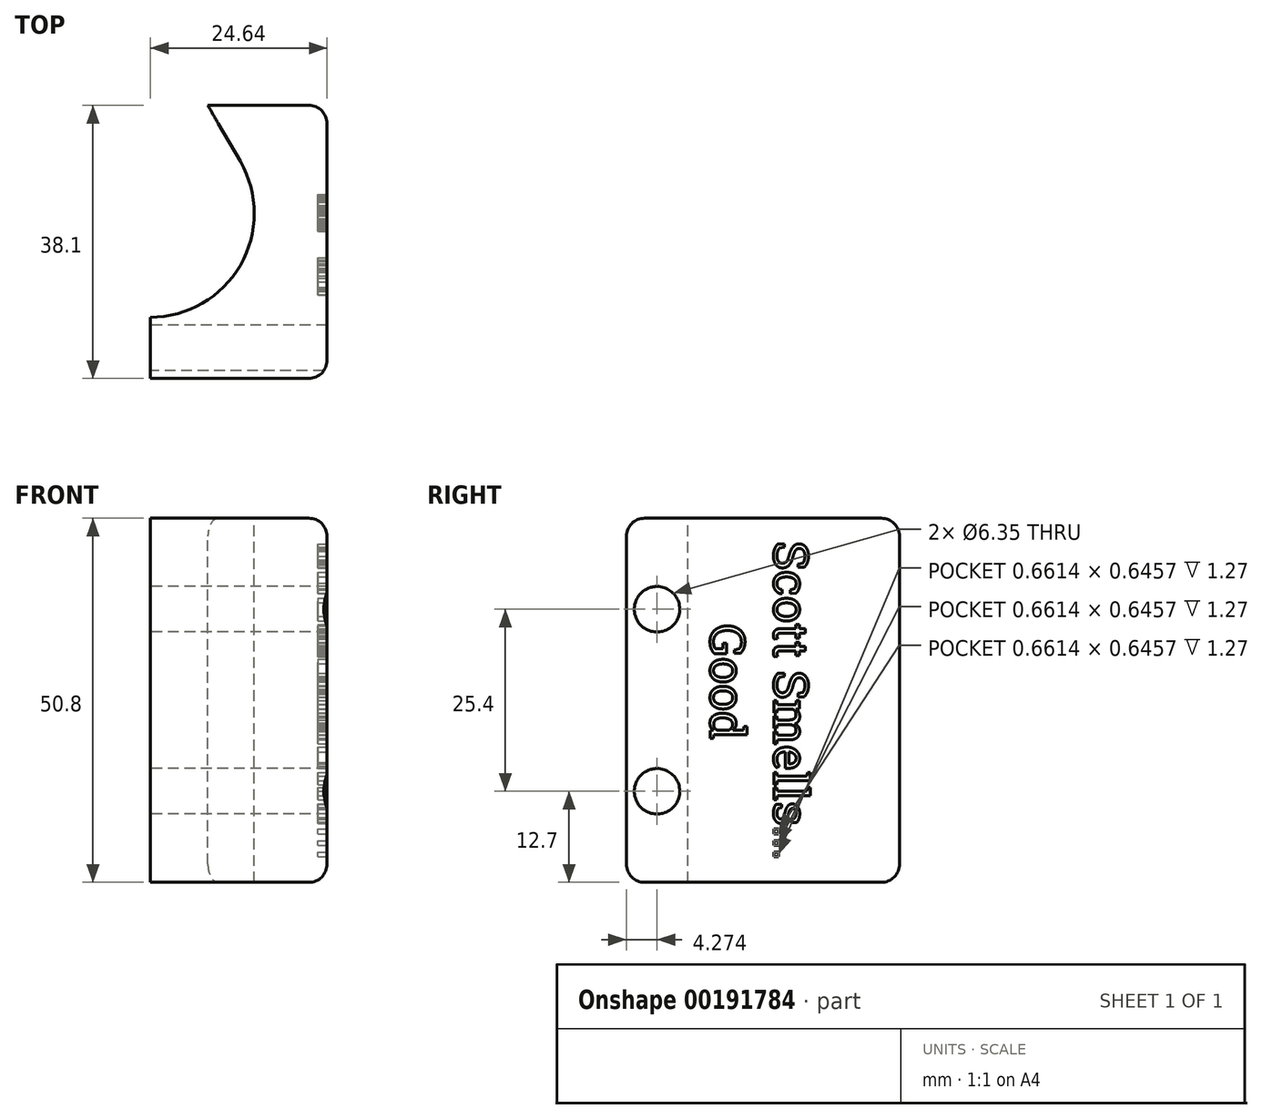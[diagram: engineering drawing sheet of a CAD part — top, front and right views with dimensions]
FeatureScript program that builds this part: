
annotation { "Feature Type Name" : "Feature", "Feature Type Description" : "" }
export const myFeature = defineFeature(function(context is Context, id is Id, definition is map)
    precondition{}
    {
        {
            var Q0;
            Q0=qCreatedBy(makeId("Top.planeOp"),FACE);
            var sketch = newSketch(context, id + "F0", { "sketchPlane" : qUnion([Q0])});
            skLineSegment(sketch, "E0.bottom", {"start": v(-23.12, 21.63) * mm, "end": v(1.52, 21.63) * mm});
            skLineSegment(sketch, "E0.top", {"start": v(-23.12, -16.47) * mm, "end": v(1.52, -16.47) * mm});
            skLineSegment(sketch, "E0.left", {"start": v(-23.12, 21.63) * mm, "end": v(-23.12, -16.47) * mm});
            skLineSegment(sketch, "E0.right", {"start": v(1.52, 21.63) * mm, "end": v(1.52, -16.47) * mm});
            skSolve(sketch);
        }
        {
            var Q0;
            Q0=makeQuery(id+"F0.imprint","IMPRINT",FACE,{"disambiguationData":[TD([[makeQuery(id+"F0.imprint","IMPRINT",EDGE,{"derivedFrom":sQuery(id+"F0.wireOp",EDGE,"E0.bottom")}),-1.0]])]});
            extrude(context, id + "F1", {"entities" : qUnion([Q0]), "depth" : 50.8 * mm});
        }
        {
            var Q0;
            Q0=makeQuery(id+"F1.opExtrude","CAP_FACE",FACE,{"disambiguationData":[OSD([sQuery(id+"F0.wireOp",EDGE,"E0.bottom"),sQuery(id+"F0.wireOp",EDGE,"E0.top"),sQuery(id+"F0.wireOp",EDGE,"E0.left"),sQuery(id+"F0.wireOp",EDGE,"E0.right")])],"isStart":false});
            var sketch = newSketch(context, id + "F2", { "sketchPlane" : qUnion([Q0])});
            skArc(sketch, "E1", {"start": v(-35.08, 14.71) * mm, "mid": v(-23.65, -7.91) * mm, "end": v(-10.59, 13.8) * mm});
            skLineSegment(sketch, "E2", {"start": v(-31.12, 21.63) * mm, "end": v(-15.12, 21.63) * mm});
            skLineSegment(sketch, "E3", {"start": v(-31.12, 21.63) * mm, "end": v(-36.21, 12.73) * mm});
            skLineSegment(sketch, "E4", {"start": v(-15.12, 21.63) * mm, "end": v(-10.59, 13.8) * mm});
            skSolve(sketch);
        }
        {
            var Q0;
            Q0 = qSketchRegion(id + "F2", true);
            extrude(context, id + "F3", {"entities" : qUnion([Q0]), "operationType" : NewBodyOperationType.REMOVE, "oppositeDirection" : true, "depth" : 76.2 * mm});
        }
        {
            var Q0;
            Q0=makeQuery(id+"F1.opExtrude","SWEPT_FACE",FACE,{"disambiguationData":[OSD([sQuery(id+"F0.wireOp",EDGE,"E0.left")])]});
            var sketch = newSketch(context, id + "F4", { "sketchPlane" : qUnion([Q0])});
            skCircle(sketch, "E5", {"center": v(12.2, 38.1) * mm, "radius": 3.18 * mm});
            skCircle(sketch, "E6", {"center": v(12.2, 12.7) * mm, "radius": 3.18 * mm});
            skSolve(sketch);
        }
        {
            var Q0;
            Q0=makeQuery(id+"F1.opExtrude","CAP_EDGE",EDGE,{"disambiguationData":[OSD([sQuery(id+"F0.wireOp",EDGE,"E0.right")])],"isStart":false});
            var Q1;
            Q1=makeQuery(id+"F1.opExtrude","CAP_EDGE",EDGE,{"disambiguationData":[OSD([sQuery(id+"F0.wireOp",EDGE,"E0.right")])],"isStart":true});
            var Q2;
            Q2=makeQuery(id+"F1.opExtrude","SWEPT_EDGE",EDGE,{"disambiguationData":[OSD([sQuery(id+"F0.wireOp",EDGE,"E0.top"),sQuery(id+"F0.wireOp",EDGE,"E0.right")])]});
            var Q3;
            Q3=makeQuery(id+"F1.opExtrude","SWEPT_EDGE",EDGE,{"disambiguationData":[OSD([sQuery(id+"F0.wireOp",EDGE,"E0.bottom"),sQuery(id+"F0.wireOp",EDGE,"E0.right")])]});
            var Q4;
            Q4=makeQuery(id+"F1.opExtrude","CAP_EDGE",EDGE,{"disambiguationData":[OSD([sQuery(id+"F0.wireOp",EDGE,"E0.top")])],"isStart":false});
            var Q5;
            Q5=makeQuery(id+"F1.opExtrude","CAP_EDGE",EDGE,{"disambiguationData":[OSD([sQuery(id+"F0.wireOp",EDGE,"E0.bottom")])],"isStart":false});
            var Q6;
            Q6=makeQuery(id+"F1.opExtrude","CAP_EDGE",EDGE,{"disambiguationData":[OSD([sQuery(id+"F0.wireOp",EDGE,"E0.bottom")])],"isStart":true});
            var Q7;
            Q7=makeQuery(id+"F1.opExtrude","CAP_EDGE",EDGE,{"disambiguationData":[OSD([sQuery(id+"F0.wireOp",EDGE,"E0.top")])],"isStart":true});
            fillet(context, id + "F5", {"entities" : qUnion([Q0, Q1, Q2, Q3, Q4, Q5, Q6, Q7]), "radius" : 2.54 * mm, "tangentPropagation" : true, "allowEdgeOverflow" : false});
        }
        {
            var Q0;
            Q0=makeQuery(id+"F1.opExtrude","SWEPT_FACE",FACE,{"disambiguationData":[OSD([sQuery(id+"F0.wireOp",EDGE,"E0.right")])]});
            var sketch = newSketch(context, id + "F6", { "sketchPlane" : qUnion([Q0])});
            skText(sketch, "E7", { "text": "Scott Smells... \n       Good", "fontName": "RobotoSlab-Regular.ttf"});
            const initialGuessF6  = {"E7": [0.0041, 0.04763, 0, -1, 0.00483]};
            skSetInitialGuess(sketch, initialGuessF6);
            skSolve(sketch);
        }
        {
            var Q0;
            Q0 = qSketchRegion(id + "F6", true);
            extrude(context, id + "F7", {"entities" : qUnion([Q0]), "operationType" : NewBodyOperationType.REMOVE, "oppositeDirection" : true, "depth" : 1.27 * mm});
        }
        {
            var Q0;
            Q0 = qSketchRegion(id + "F4", true);
            extrude(context, id + "F8", {"entities" : qUnion([Q0]), "operationType" : NewBodyOperationType.REMOVE, "oppositeDirection" : true, "depth" : 25.4 * mm});
        }
    });
